SOLIDWORKS PART (.sldprt)
format: sldprt  version: not decoded by parser v0  size: 259,584 bytes
history: native  units: mm
features: plane x24, sketch x21, cut_revolve x12, cut_extrude x8, material x1, extrude x1, thread x1 (+10 scaffold rows collapsed)
feature tree (78):
  scaffold x10  (default folders/planes/origin — collapsed)
  material  "材质 <未指定>"
  plane  "前视基准面"
  plane  "上视基准面"
  plane  "右视基准面"
  plane  "基准面4"
  sketch  "草图1"
  extrude  "凸台-拉伸1"  Depth=43mm
  plane  "基准面5"
  sketch  "草图2"
  cut_revolve  "切除-旋转1"  [1 undecoded]
  thread  "装饰螺纹线1"  Diameter=15mm  [1 undecoded]
  plane  "基准面6"
  sketch  "草图3"
  cut_revolve  "切除-旋转2"  Angle=360deg
  plane  "基准面7"
  sketch  "草图4"
  cut_extrude  "切除-拉伸1"  Depth=4mm
  plane  "基准面8"
  sketch  "草图5"
  cut_extrude  "切除-拉伸2"  Depth=4mm
  plane  "基准面9"
  sketch  "草图6"
  cut_revolve  "切除-旋转3"  Angle=360deg
  plane  "基准面10"
  sketch  "草图7"
  cut_revolve  "切除-旋转4"  Angle=360deg
  plane  "基准面11"
  sketch  "草图8"
  cut_revolve  "切除-旋转5"  Angle=360deg
  plane  "基准面12"
  sketch  "草图9"
  cut_revolve  "切除-旋转6"  Angle=360deg
  plane  "基准面13"
  sketch  "草图10"
  cut_revolve  "切除-旋转7"  Angle=360deg
  plane  "基准面14"
  sketch  "草图11"
  cut_revolve  "切除-旋转8"  Angle=360deg
  plane  "基准面15"
  sketch  "草图12"
  cut_revolve  "切除-旋转9"  Angle=360deg
  plane  "基准面16"
  sketch  "草图13"
  cut_revolve  "切除-旋转10"  Angle=360deg
  plane  "基准面17"
  sketch  "草图14"
  cut_extrude  "切除-拉伸3"  Depth=1.6mm
  plane  "基准面18"
  sketch  "草图15"
  cut_extrude  "切除-拉伸4"  Depth=1.6mm
  plane  "基准面19"
  sketch  "草图16"
  cut_extrude  "切除-拉伸5"  Depth=1.5mm
  plane  "基准面20"
  sketch  "草图17"
  cut_extrude  "切除-拉伸6"  Depth=1.5mm
  plane  "基准面21"
  sketch  "草图18"
  cut_revolve  "切除-旋转11"  Angle=360deg
  plane  "基准面22"
  sketch  "草图19"
  cut_revolve  "切除-旋转12"  Angle=360deg
  plane  "基准面23"
  sketch  "草图20"
  cut_extrude  "切除-拉伸7"  Depth=1.5mm
  plane  "基准面24"
  sketch  "草图21"
  cut_extrude  "切除-拉伸8"  Depth=1.5mm
decode coverage: 21 of 43 modeling features carry decoded parameters
note: 2 parameter values undecoded
note: suppression state not decoded; provenance and decode notes live in map.json
